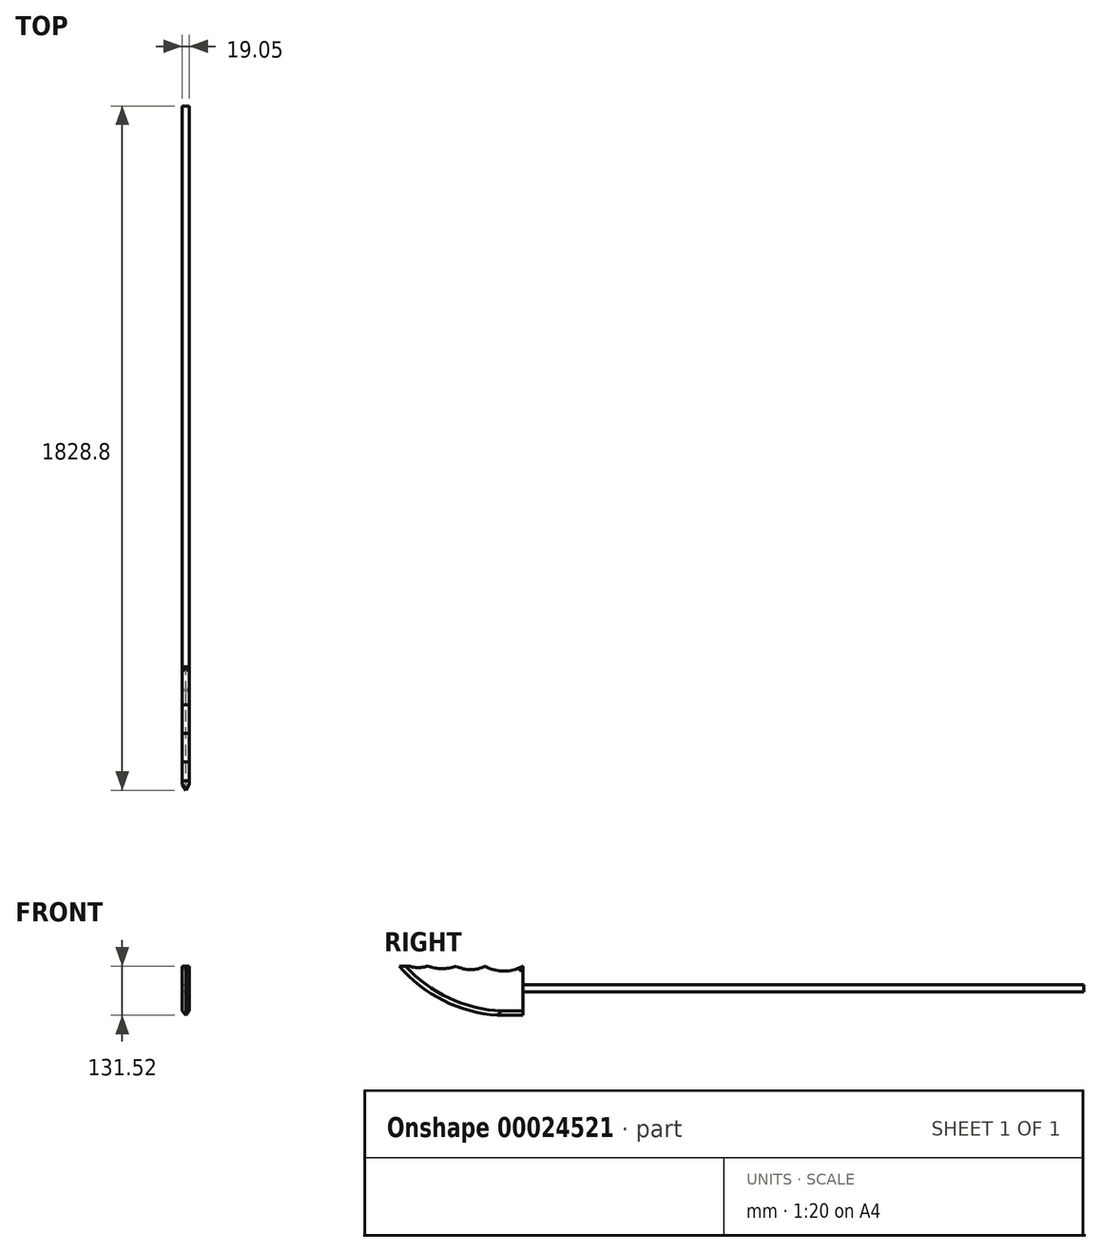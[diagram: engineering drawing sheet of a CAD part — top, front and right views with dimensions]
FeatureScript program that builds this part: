
annotation { "Feature Type Name" : "Feature", "Feature Type Description" : "" }
export const myFeature = defineFeature(function(context is Context, id is Id, definition is map)
    precondition{}
    {
        {
            var Q0;
            Q0=qCreatedBy(makeId("Right.planeOp"),FACE);
            var sketch = newSketch(context, id + "F0", { "sketchPlane" : qUnion([Q0])});
            skLineSegment(sketch, "E0", {"start": v(0, 0) * mm, "end": v(914.4, 0) * mm});
            skArc(sketch, "E1", {"start": v(0, 0) * mm, "mid": v(117.9, -92.03) * mm, "end": v(262.16, -131.52) * mm});
            skLineSegment(sketch, "E2", {"start": v(262.16, -131.52) * mm, "end": v(914.4, -131.52) * mm});
            skLineSegment(sketch, "E3", {"start": v(914.4, 0) * mm, "end": v(914.4, -131.52) * mm});
            skSolve(sketch);
        }
        {
            var Q0;
            Q0 = qSketchRegion(id + "F0", true);
            extrude(context, id + "F1", {"entities" : qUnion([Q0]), "depth" : 19.05 * mm});
        }
        {
            var Q0;
            Q0=makeQuery(id+"F1.opExtrude","SWEPT_FACE",FACE,{"disambiguationData":[OSD([sQuery(id+"F0.wireOp",EDGE,"E0")])]});
            var sketch = newSketch(context, id + "F2", { "sketchPlane" : qUnion([Q0])});
            skLineSegment(sketch, "E4", {"start": v(9.53, 0) * mm, "end": v(0, 16.5) * mm});
            skLineSegment(sketch, "E5", {"start": v(9.53, 0) * mm, "end": v(19.05, 16.5) * mm});
            skLineSegment(sketch, "E6", {"start": v(19.05, 16.5) * mm, "end": v(19.05, 0) * mm});
            skLineSegment(sketch, "E7", {"start": v(19.05, 0) * mm, "end": v(0, 0) * mm});
            skLineSegment(sketch, "E8", {"start": v(0, 0) * mm, "end": v(0, 16.5) * mm});
            skSolve(sketch);
        }
        {
            var Q0;
            {var subQ0=sQuery(id+"F2.wireOp",EDGE,"E4");Q0=makeQuery(id+"F2.imprint","IMPRINT",FACE,{"disambiguationData":[TD([[makeQuery(id+"F2.imprint","IMPRINT",EDGE,{"derivedFrom":subQ0}),1.0]])]});}
            var Q1;
            {var subQ0=sQuery(id+"F2.wireOp",EDGE,"E5");Q1=makeQuery(id+"F2.imprint","IMPRINT",FACE,{"disambiguationData":[TD([[makeQuery(id+"F2.imprint","IMPRINT",EDGE,{"derivedFrom":subQ0}),-1.0]])]});}
            var Q2;
            Q2=makeQuery(id+"F1.opExtrude","CAP_EDGE",EDGE,{"disambiguationData":[OSD([sQuery(id+"F0.wireOp",EDGE,"E1")])],"isStart":false});
            sweep(context, id + "F3", {"operationType" : NewBodyOperationType.REMOVE, "profiles" : qUnion([Q0, Q1]), "path" : qUnion([Q2])});
        }
        {
            var Q0;
            Q0=makeQuery(id+"F3.boolean.opBoolean","COPY",FACE,{"derivedFrom":makeQuery(id+"F3.opSweep","CAP_FACE",FACE,{"disambiguationData":[OSD([sQuery(id+"F0.wireOp",EDGE,"E1"),sQuery(id+"F0.wireOp",EDGE,"E2"),sQuery(id+"F2.wireOp",EDGE,"E5"),sQuery(id+"F2.wireOp",EDGE,"E6"),sQuery(id+"F2.wireOp",EDGE,"E7")])],"isStart":false})});
            var Q1;
            Q1=makeQuery(id+"F3.boolean.opBoolean","COPY",FACE,{"derivedFrom":makeQuery(id+"F3.opSweep","CAP_FACE",FACE,{"disambiguationData":[OSD([sQuery(id+"F0.wireOp",EDGE,"E1"),sQuery(id+"F0.wireOp",EDGE,"E2"),sQuery(id+"F2.wireOp",EDGE,"E4"),sQuery(id+"F2.wireOp",EDGE,"E7"),sQuery(id+"F2.wireOp",EDGE,"E8")])],"isStart":false})});
            var Q2;
            Q2=makeQuery(id+"F1.opExtrude","CAP_EDGE",EDGE,{"disambiguationData":[OSD([sQuery(id+"F0.wireOp",EDGE,"E2")])],"isStart":true});
            sweep(context, id + "F4", {"operationType" : NewBodyOperationType.REMOVE, "profiles" : qUnion([Q0, Q1]), "path" : qUnion([Q2])});
        }
        {
            var Q0;
            Q0=makeQuery(id+"F1.opExtrude","SWEPT_FACE",FACE,{"disambiguationData":[OSD([sQuery(id+"F0.wireOp",EDGE,"E3")])]});
            var sketch = newSketch(context, id + "F5", { "sketchPlane" : qUnion([Q0])});
            skLineSegment(sketch, "E9", {"start": v(-9.53, -131.52) * mm, "end": v(-9.53, 0) * mm});
            skLineSegment(sketch, "E10", {"start": v(-19.05, -59.9) * mm, "end": v(0, -59.9) * mm});
            skCircle(sketch, "E11", {"center": v(-9.53, -59.9) * mm, "radius": 9.53 * mm});
            skSolve(sketch);
        }
        {
            var Q0;
            Q0 = qSketchRegion(id + "F5", true);
            extrude(context, id + "F6", {"entities" : qUnion([Q0]), "depth" : 2743.2 * mm});
        }
        {
            var Q0;
            Q0=makeQuery(id+"F1.opExtrude","SWEPT_FACE",FACE,{"disambiguationData":[OSD([sQuery(id+"F0.wireOp",EDGE,"E3")])]});
            extrude(context, id + "F7", {"entities" : qUnion([Q0]), "operationType" : NewBodyOperationType.REMOVE, "oppositeDirection" : true, "depth" : 584.2 * mm});
        }
        {
            var Q0;
            Q0=makeQuery(id+"F6.opExtrude","CAP_FACE",FACE,{"disambiguationData":[OSD([sQuery(id+"F5.wireOp",EDGE,"E11")])],"isStart":true});
            extrude(context, id + "F8", {"entities" : qUnion([Q0]), "operationType" : NewBodyOperationType.ADD, "depth" : 584.2 * mm});
        }
        {
            var Q0;
            Q0=makeQuery(id+"F6.opExtrude","CAP_FACE",FACE,{"disambiguationData":[OSD([sQuery(id+"F5.wireOp",EDGE,"E11")])],"isStart":false});
            extrude(context, id + "F9", {"entities" : qUnion([Q0]), "operationType" : NewBodyOperationType.REMOVE, "oppositeDirection" : true, "depth" : 1828.8 * mm});
        }
        {
            var Q0;
            Q0=makeQuery(id+"F1.opExtrude","CAP_FACE",FACE,{"disambiguationData":[OSD([sQuery(id+"F0.wireOp",EDGE,"E0"),sQuery(id+"F0.wireOp",EDGE,"E1"),sQuery(id+"F0.wireOp",EDGE,"E2"),sQuery(id+"F0.wireOp",EDGE,"E3")])],"isStart":true});
            var sketch = newSketch(context, id + "F10", { "sketchPlane" : qUnion([Q0])});
            skArc(sketch, "E12", {"start": v(-330.2, 0) * mm, "mid": v(-279.4, -13.61) * mm, "end": v(-228.6, 0) * mm});
            skLineSegment(sketch, "E13", {"start": v(-330.2, 0) * mm, "end": v(-228.6, 0) * mm});
            skLineSegment(sketch, "E14", {"start": v(-228.6, 0) * mm, "end": v(-152.4, 0) * mm});
            skLineSegment(sketch, "E15", {"start": v(-152.4, 0) * mm, "end": v(-76.2, 0) * mm});
            skLineSegment(sketch, "E16", {"start": v(-76.2, 0) * mm, "end": v(-25.4, 0) * mm});
            skArc(sketch, "E17", {"start": v(-228.6, 0) * mm, "mid": v(-190.5, -9.8) * mm, "end": v(-152.4, 0) * mm});
            skArc(sketch, "E18", {"start": v(-152.4, 0) * mm, "mid": v(-114.3, -6.9) * mm, "end": v(-76.2, 0) * mm});
            skArc(sketch, "E19", {"start": v(-76.2, 0) * mm, "mid": v(-50.8, -3.8) * mm, "end": v(-25.4, 0) * mm});
            skSolve(sketch);
        }
        {
            var Q0;
            Q0 = qSketchRegion(id + "F10", true);
            extrude(context, id + "F11", {"entities" : qUnion([Q0]), "operationType" : NewBodyOperationType.REMOVE, "oppositeDirection" : true, "depth" : 25.4 * mm});
        }
        {
            var Q0;
            Q0=makeQuery(id+"F7.boolean.opBoolean","COPY",FACE,{"derivedFrom":makeQuery(id+"F7.opExtrude","CAP_FACE",FACE,{"disambiguationData":[OSD([sQuery(id+"F0.wireOp",EDGE,"E3")])],"isStart":false})});
            var sketch = newSketch(context, id + "F12", { "sketchPlane" : qUnion([Q0])});
            skLineSegment(sketch, "E20", {"start": v(-9.53, 0) * mm, "end": v(-19.05, -11.62) * mm});
            skLineSegment(sketch, "E21", {"start": v(-9.53, 0) * mm, "end": v(0, -11.62) * mm});
            skSolve(sketch);
        }
        {
            var Q0;
            {var subQ0=sQuery(id+"F12.wireOp",EDGE,"E20");Q0=makeQuery(id+"F12.imprint","IMPRINT",FACE,{"disambiguationData":[TD([[makeQuery(id+"F12.imprint","IMPRINT",EDGE,{"derivedFrom":subQ0}),-1.0]])]});}
            var Q1;
            {var subQ0=sQuery(id+"F12.wireOp",EDGE,"E21");Q1=makeQuery(id+"F12.imprint","IMPRINT",FACE,{"disambiguationData":[TD([[makeQuery(id+"F12.imprint","IMPRINT",EDGE,{"derivedFrom":subQ0}),1.0]])]});}
            var Q2;
            Q2=makeQuery(id+"F11.boolean.opBoolean","COPY",EDGE,{"derivedFrom":makeQuery(id+"F11.opExtrude","CAP_EDGE",EDGE,{"disambiguationData":[OSD([sQuery(id+"F10.wireOp",EDGE,"E12")])],"isStart":true})});
            var Q3;
            Q3=makeQuery(id+"F11.boolean.opBoolean","COPY",EDGE,{"derivedFrom":makeQuery(id+"F11.opExtrude","CAP_EDGE",EDGE,{"disambiguationData":[OSD([sQuery(id+"F10.wireOp",EDGE,"E17")])],"isStart":true})});
            var Q4;
            Q4=makeQuery(id+"F11.boolean.opBoolean","COPY",EDGE,{"derivedFrom":makeQuery(id+"F11.opExtrude","CAP_EDGE",EDGE,{"disambiguationData":[OSD([sQuery(id+"F10.wireOp",EDGE,"E18")])],"isStart":true})});
            var Q5;
            Q5=makeQuery(id+"F11.boolean.opBoolean","COPY",EDGE,{"derivedFrom":makeQuery(id+"F11.opExtrude","CAP_EDGE",EDGE,{"disambiguationData":[OSD([sQuery(id+"F10.wireOp",EDGE,"E19")])],"isStart":true})});
            var Q6;
            Q6=makeQuery(id+"F1.opExtrude","CAP_EDGE",EDGE,{"disambiguationData":[OSD([sQuery(id+"F0.wireOp",EDGE,"E0")])],"isStart":true});
            var Q7;
            Q7=makeQuery(id+"F3.boolean.opBoolean","COPY",EDGE,{"derivedFrom":makeQuery(id+"F3.opSweep","CAP_EDGE",EDGE,{"disambiguationData":[OSD([sQuery(id+"F0.wireOp",EDGE,"E0"),sQuery(id+"F0.wireOp",EDGE,"E1"),sQuery(id+"F2.wireOp",EDGE,"E4")])],"isStart":true})});
            sweep(context, id + "F13", {"operationType" : NewBodyOperationType.REMOVE, "profiles" : qUnion([Q0, Q1]), "path" : qUnion([Q2, Q3, Q4, Q5, Q6, Q7])});
        }
    });
